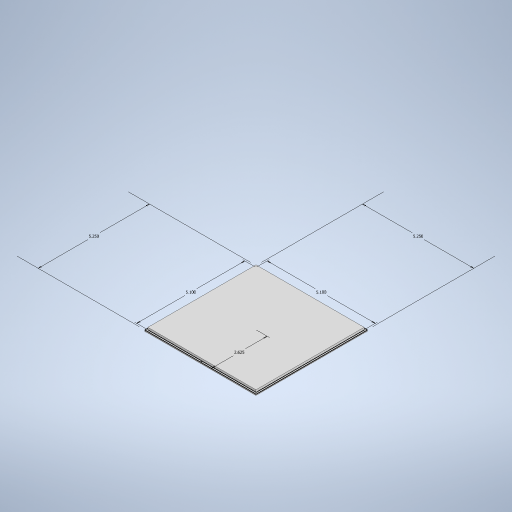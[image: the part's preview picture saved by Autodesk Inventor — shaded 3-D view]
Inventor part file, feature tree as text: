
AUTODESK INVENTOR PART (.ipt)
format: ipt  version: 2024.1 (Build 281209000, 209)  size: 259,584 bytes
history: native  units: in
note: dims shown in document units (in); Inventor stores cm internally (conversion verified against a paired STEP export)
features: extrude x2, sketch x1, fillet x1
ambient origin geometry x8: Origin, YZ Plane, XZ Plane, XY Plane, X Axis, Y Axis, Z Axis, Center Point
bodies: Solid1 (feature_tree)
feature tree (4):
  sketch  "Sketch1"  dims[d0=5.25in d1=5.25in d2=2.625in d3=5.1in d4=5.1in d5=0.1in d6=0.0in d7=0.1in d8=0.0in d9=0.05in]
  extrude  "Extrusion1"  Depth=5.25in
  extrude  "Extrusion2"  Depth=0.05in
  fillet  "Fillet1"  Radius=5.1in
